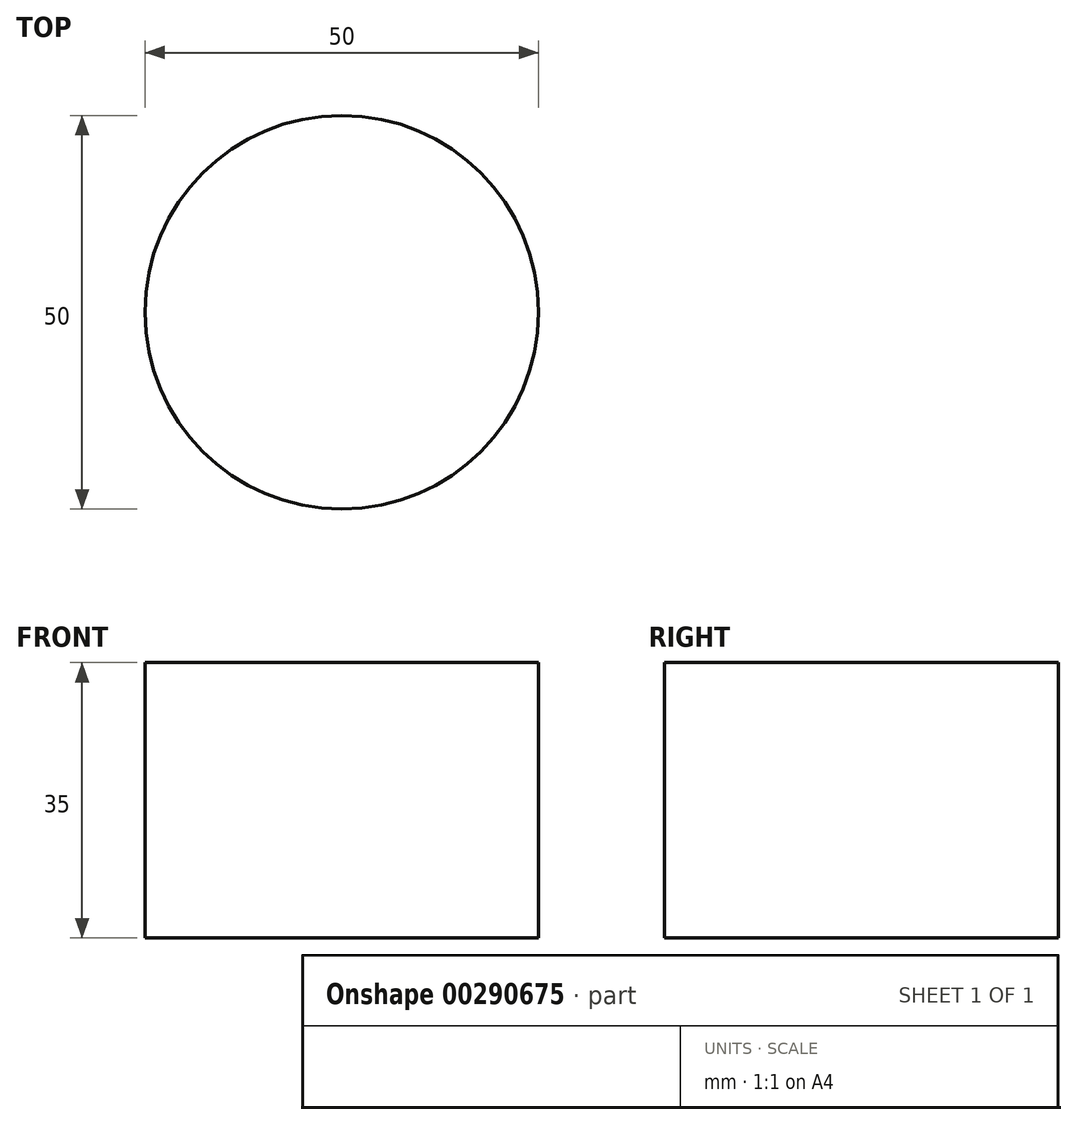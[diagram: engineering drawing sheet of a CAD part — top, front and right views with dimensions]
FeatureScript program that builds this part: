
annotation { "Feature Type Name" : "Feature", "Feature Type Description" : "" }
export const myFeature = defineFeature(function(context is Context, id is Id, definition is map)
    precondition{}
    {
        {
            var Q0;
            Q0=qCreatedBy(makeId("Right.planeOp"),FACE);
            var sketch = newSketch(context, id + "F0", { "sketchPlane" : qUnion([Q0])});
            skLineSegment(sketch, "E0.bottom", {"start": v(0, 35) * mm, "end": v(25, 35) * mm});
            skLineSegment(sketch, "E0.top", {"start": v(0, 0) * mm, "end": v(25, 0) * mm});
            skLineSegment(sketch, "E0.left", {"start": v(0, 35) * mm, "end": v(0, 0) * mm});
            skLineSegment(sketch, "E0.right", {"start": v(25, 35) * mm, "end": v(25, 0) * mm});
            skLineSegment(sketch, "E1", {"start": v(0, 61.44) * mm, "end": v(0, -29) * mm, "construction": true});
            skSolve(sketch);
        }
        {
            var Q0;
            Q0=makeQuery(id+"F0.imprint","IMPRINT",FACE,{"disambiguationData":[TD([[makeQuery(id+"F0.imprint","IMPRINT",EDGE,{"derivedFrom":sQuery(id+"F0.wireOp",EDGE,"E0.bottom")}),-1.0]])]});
            var Q1;
            Q1=sQuery(id+"F0.wireOp",EDGE,"E1");
            revolve(context, id + "F1", {"entities" : qUnion([Q0]), "axis" : qUnion([Q1]), "revolveType" : RevolveType.FULL});
        }
    });
